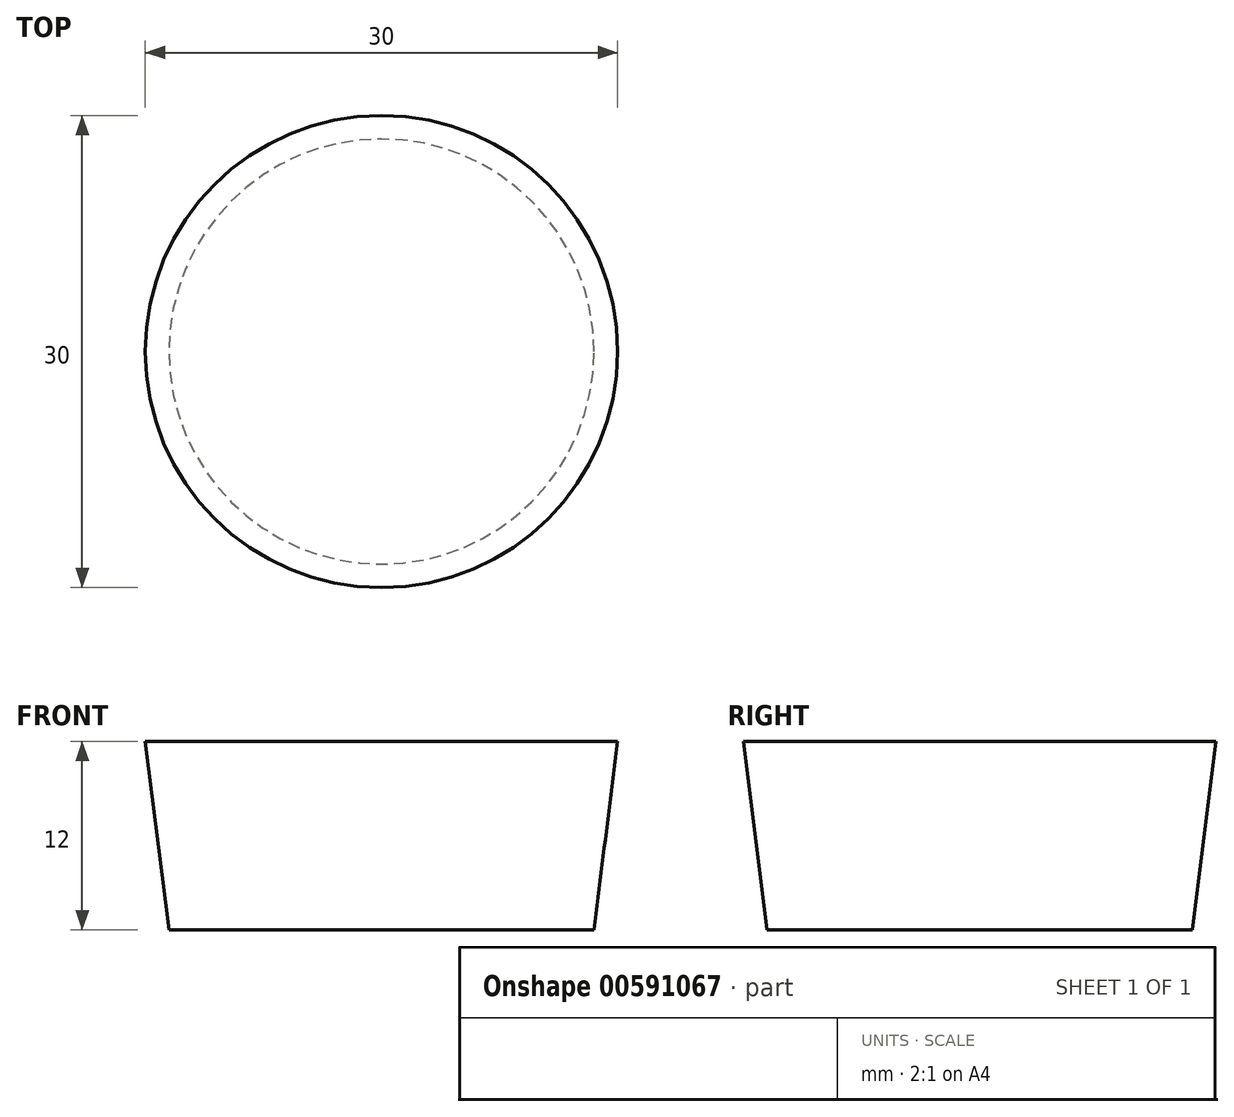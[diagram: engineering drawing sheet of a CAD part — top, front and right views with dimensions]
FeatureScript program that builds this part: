
annotation { "Feature Type Name" : "Feature", "Feature Type Description" : "" }
export const myFeature = defineFeature(function(context is Context, id is Id, definition is map)
    precondition{}
    {
        {
            var Q0;
            Q0=qCreatedBy(makeId("Top.planeOp"),FACE);
            cPlane(context, id + "F0", {"entities" : qUnion([Q0]), "cplaneType" : CPlaneType.OFFSET, "offset" : 12 * mm, "width" : 150 * mm, "height" : 150 * mm});
        }
        {
            var Q0;
            Q0=qCreatedBy(makeId("Top.planeOp"),FACE);
            var sketch = newSketch(context, id + "F1", { "sketchPlane" : qUnion([Q0])});
            skCircle(sketch, "E0", {"center": v(0, 0) * mm, "radius": 13.5 * mm});
            skSolve(sketch);
        }
        {
            var Q0;
            Q0=qCreatedBy(id+"F0.planeOp",FACE);
            var sketch = newSketch(context, id + "F2", { "sketchPlane" : qUnion([Q0])});
            skCircle(sketch, "E1", {"center": v(0, 0) * mm, "radius": 15 * mm});
            skSolve(sketch);
        }
        {
            var Q0;
            Q0=makeQuery(id+"F1.imprint","IMPRINT",FACE,{"disambiguationData":[TD([[makeQuery(id+"F1.imprint","IMPRINT",EDGE,{"derivedFrom":sQuery(id+"F1.wireOp",EDGE,"E0")}),1.0]])]});
            var Q1;
            Q1=makeQuery(id+"F2.imprint","IMPRINT",FACE,{"disambiguationData":[TD([[makeQuery(id+"F2.imprint","IMPRINT",EDGE,{"derivedFrom":sQuery(id+"F2.wireOp",EDGE,"E1")}),1.0]])]});
            loft(context, id + "F3", {"sheetProfilesArray" : [{ "sheetProfileEntities" : qUnion([Q0]) }, { "sheetProfileEntities" : qUnion([Q1]) }]});
        }
    });
